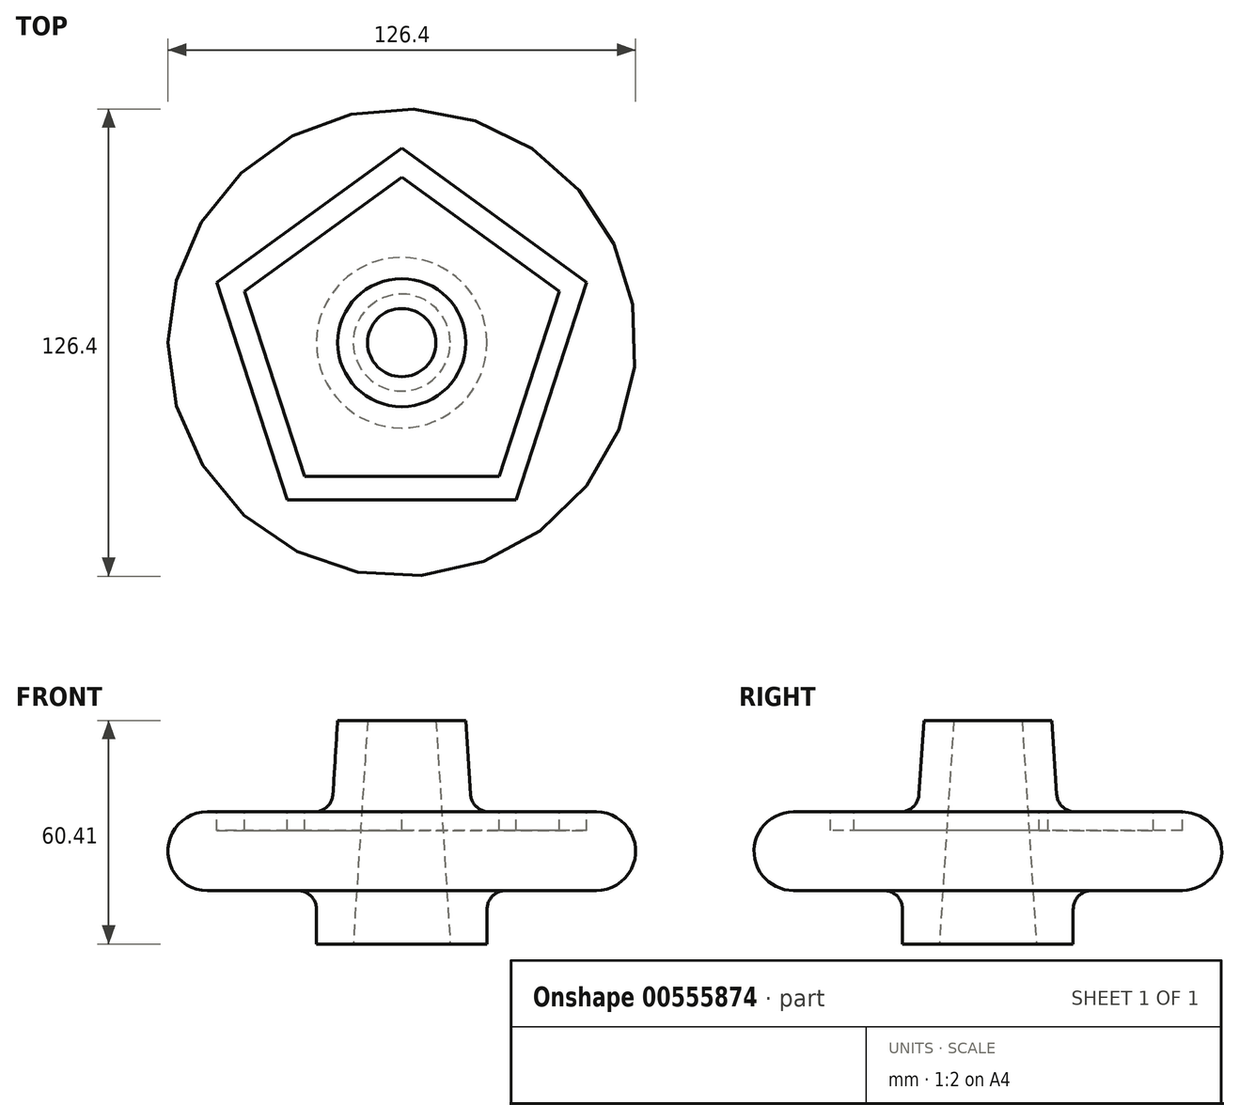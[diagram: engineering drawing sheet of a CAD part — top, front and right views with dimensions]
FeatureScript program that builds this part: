
annotation { "Feature Type Name" : "Feature", "Feature Type Description" : "" }
export const myFeature = defineFeature(function(context is Context, id is Id, definition is map)
    precondition{}
    {
        {
            var Q0;
            Q0=qCreatedBy(makeId("Front.planeOp"),FACE);
            var sketch = newSketch(context, id + "F0", { "sketchPlane" : qUnion([Q0])});
            skLineSegment(sketch, "E0", {"start": v(0, 0) * mm, "end": v(0, 47.92) * mm, "construction": true});
            skLineSegment(sketch, "E1", {"start": v(-9.23, 60.41) * mm, "end": v(-13.11, 0) * mm});
            skLineSegment(sketch, "E2", {"start": v(-13.11, 0) * mm, "end": v(-23.06, 0) * mm});
            skLineSegment(sketch, "E3", {"start": v(-23.06, 0) * mm, "end": v(-23.06, 14.47) * mm});
            skLineSegment(sketch, "E4", {"start": v(-23.06, 14.47) * mm, "end": v(-52.58, 14.47) * mm});
            skArc(sketch, "E5", {"start": v(-52.58, 14.47) * mm, "mid": v(-63.2, 25.1) * mm, "end": v(-52.58, 35.72) * mm});
            skLineSegment(sketch, "E6", {"start": v(-52.58, 35.72) * mm, "end": v(-18.9, 35.72) * mm});
            skLineSegment(sketch, "E7", {"start": v(-18.9, 35.72) * mm, "end": v(-17.32, 60.41) * mm});
            skLineSegment(sketch, "E8", {"start": v(-17.32, 60.41) * mm, "end": v(-9.23, 60.41) * mm});
            skSolve(sketch);
        }
        {
            var Q0;
            Q0=makeQuery(id+"F0.imprint","IMPRINT",FACE,{"disambiguationData":[TD([[makeQuery(id+"F0.imprint","IMPRINT",EDGE,{"derivedFrom":sQuery(id+"F0.wireOp",EDGE,"E1")}),-1.0]])]});
            var Q1;
            Q1=sQuery(id+"F0.wireOp",EDGE,"E0");
            revolve(context, id + "F1", {"entities" : qUnion([Q0]), "axis" : qUnion([Q1]), "revolveType" : RevolveType.FULL});
        }
        {
            var Q0;
            Q0=makeQuery(id+"F1.opRevolve","SWEPT_EDGE",EDGE,{"disambiguationData":[OSD([sQuery(id+"F0.wireOp",EDGE,"E6"),sQuery(id+"F0.wireOp",EDGE,"E7")])]});
            var Q1;
            Q1=makeQuery(id+"F1.opRevolve","SWEPT_EDGE",EDGE,{"disambiguationData":[OSD([sQuery(id+"F0.wireOp",EDGE,"E3"),sQuery(id+"F0.wireOp",EDGE,"E4")])]});
            fillet(context, id + "F2", {"entities" : qUnion([Q0, Q1]), "radius" : 5.08 * mm, "tangentPropagation" : true, "allowEdgeOverflow" : false});
        }
        {
            var Q0;
            Q0=makeQuery(id+"F1.opRevolve","SWEPT_FACE",FACE,{"disambiguationData":[OSD([sQuery(id+"F0.wireOp",EDGE,"E6")])]});
            var sketch = newSketch(context, id + "F3", { "sketchPlane" : qUnion([Q0])});
            skCircle(sketch, "E9.cCircle", {"center": v(0, 0) * mm, "radius": 42.54 * mm, "construction": true});
            skLineSegment(sketch, "E9.0", {"start": v(50, 16.25) * mm, "end": v(30.9, -42.54) * mm});
            skLineSegment(sketch, "E9.1", {"start": v(30.9, -42.54) * mm, "end": v(-30.9, -42.54) * mm});
            skLineSegment(sketch, "E9.2", {"start": v(-30.9, -42.54) * mm, "end": v(-50, 16.25) * mm});
            skLineSegment(sketch, "E9.3", {"start": v(-50, 16.25) * mm, "end": v(0, 52.58) * mm});
            skLineSegment(sketch, "E9.4", {"start": v(0, 52.58) * mm, "end": v(50, 16.25) * mm});
            skPoint(sketch, "E9.0.midPoint", {"position": v(40.46, -13.14) * mm});
            skLineSegment(sketch, "E10.0", {"start": v(0, 44.73) * mm, "end": v(42.54, 13.82) * mm});
            skLineSegment(sketch, "E10.1", {"start": v(-42.54, 13.82) * mm, "end": v(0, 44.73) * mm});
            skLineSegment(sketch, "E10.2", {"start": v(42.54, 13.82) * mm, "end": v(26.3, -36.19) * mm});
            skLineSegment(sketch, "E10.3", {"start": v(26.3, -36.19) * mm, "end": v(-26.3, -36.19) * mm});
            skLineSegment(sketch, "E10.4", {"start": v(-26.3, -36.19) * mm, "end": v(-42.54, 13.82) * mm});
            skSolve(sketch);
        }
        {
            var Q0;
            Q0=makeQuery(id+"F3.imprint","IMPRINT",FACE,{"disambiguationData":[TD([[makeQuery(id+"F3.imprint","IMPRINT",EDGE,{"derivedFrom":sQuery(id+"F3.wireOp",EDGE,"E9.0")}),-1.0]])]});
            extrude(context, id + "F4", {"entities" : qUnion([Q0]), "operationType" : NewBodyOperationType.REMOVE, "oppositeDirection" : true, "depth" : 5.08 * mm, "offsetDistance" : 25.4 * mm});
        }
    });
